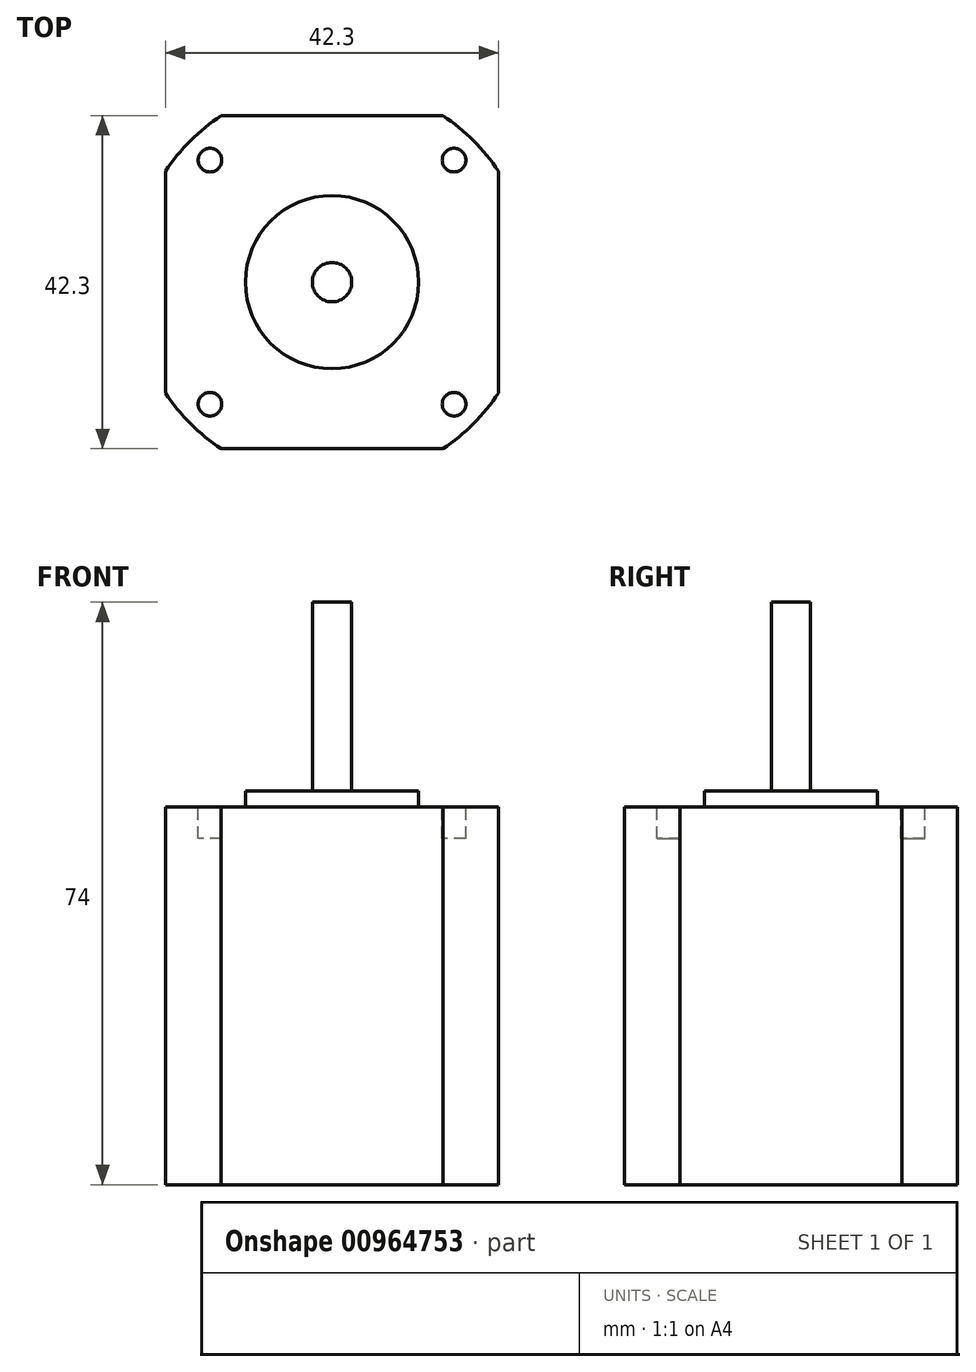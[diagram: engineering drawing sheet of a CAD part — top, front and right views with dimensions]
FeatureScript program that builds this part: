
annotation { "Feature Type Name" : "Feature", "Feature Type Description" : "" }
export const myFeature = defineFeature(function(context is Context, id is Id, definition is map)
    precondition{}
    {
        {
            var Q0;
            Q0=qCreatedBy(makeId("Top.planeOp"),FACE);
            var sketch = newSketch(context, id + "F0", { "sketchPlane" : qUnion([Q0])});
            skLineSegment(sketch, "E0.bottom", {"start": v(14.08, 21.15) * mm, "end": v(-14.08, 21.15) * mm});
            skLineSegment(sketch, "E0.top", {"start": v(14.08, -21.15) * mm, "end": v(-14.08, -21.15) * mm});
            skLineSegment(sketch, "E0.left", {"start": v(21.15, 14.08) * mm, "end": v(21.15, -14.08) * mm});
            skLineSegment(sketch, "E0.right", {"start": v(-21.15, 14.08) * mm, "end": v(-21.15, -14.08) * mm});
            skPoint(sketch, "E0.middle", {"position": v(0, 0) * mm});
            skArc(sketch, "E1", {"start": v(-14.08, 21.15) * mm, "mid": v(-17.97, 17.97) * mm, "end": v(-21.15, 14.08) * mm});
            skPoint(sketch, "E2", {"position": v(14.08, 21.15) * mm});
            skPoint(sketch, "E3", {"position": v(21.15, 14.08) * mm});
            skArc(sketch, "E4.trimOffspring", {"start": v(-21.15, -14.08) * mm, "mid": v(-17.97, -17.97) * mm, "end": v(-14.08, -21.15) * mm});
            skArc(sketch, "E5.trimOffspring", {"start": v(14.08, -21.15) * mm, "mid": v(17.97, -17.97) * mm, "end": v(21.15, -14.08) * mm});
            skArc(sketch, "E6.trimOffspring", {"start": v(21.15, 14.08) * mm, "mid": v(17.97, 17.97) * mm, "end": v(14.08, 21.15) * mm});
            skSolve(sketch);
        }
        {
            var Q0;
            Q0 = qSketchRegion(id + "F0", true);
            extrude(context, id + "F1", {"entities" : qUnion([Q0]), "depth" : 48 * mm, "offsetDistance" : 25.4 * mm});
        }
        {
            var Q0;
            Q0=makeQuery(id+"F1.opExtrude","CAP_FACE",FACE,{"disambiguationData":[OSD([sQuery(id+"F0.wireOp",EDGE,"E0.bottom"),sQuery(id+"F0.wireOp",EDGE,"E0.top"),sQuery(id+"F0.wireOp",EDGE,"E0.left"),sQuery(id+"F0.wireOp",EDGE,"E0.right"),sQuery(id+"F0.wireOp",EDGE,"E1"),sQuery(id+"F0.wireOp",EDGE,"E4.trimOffspring"),sQuery(id+"F0.wireOp",EDGE,"E5.trimOffspring"),sQuery(id+"F0.wireOp",EDGE,"E6.trimOffspring")])],"isStart":false});
            var sketch = newSketch(context, id + "F2", { "sketchPlane" : qUnion([Q0])});
            skCircle(sketch, "E7", {"center": v(0, 0) * mm, "radius": 11 * mm});
            skSolve(sketch);
        }
        {
            var Q0;
            Q0 = qSketchRegion(id + "F2", true);
            extrude(context, id + "F3", {"entities" : qUnion([Q0]), "operationType" : NewBodyOperationType.ADD, "depth" : 2 * mm, "offsetDistance" : 25.4 * mm});
        }
        {
            var Q0;
            Q0=makeQuery(id+"F3.opExtrude","CAP_FACE",FACE,{"disambiguationData":[OSD([sQuery(id+"F2.wireOp",EDGE,"E7")])],"isStart":false});
            var sketch = newSketch(context, id + "F4", { "sketchPlane" : qUnion([Q0])});
            skCircle(sketch, "E8", {"center": v(0, 0) * mm, "radius": 2.5 * mm});
            skSolve(sketch);
        }
        {
            var Q0;
            Q0 = qSketchRegion(id + "F4", true);
            extrude(context, id + "F5", {"entities" : qUnion([Q0]), "operationType" : NewBodyOperationType.ADD, "depth" : 24 * mm, "offsetDistance" : 25.4 * mm});
        }
        {
            var Q0;
            Q0=makeQuery(id+"F1.opExtrude","CAP_FACE",FACE,{"disambiguationData":[OSD([sQuery(id+"F0.wireOp",EDGE,"E0.bottom"),sQuery(id+"F0.wireOp",EDGE,"E0.top"),sQuery(id+"F0.wireOp",EDGE,"E0.left"),sQuery(id+"F0.wireOp",EDGE,"E0.right"),sQuery(id+"F0.wireOp",EDGE,"E1"),sQuery(id+"F0.wireOp",EDGE,"E4.trimOffspring"),sQuery(id+"F0.wireOp",EDGE,"E5.trimOffspring"),sQuery(id+"F0.wireOp",EDGE,"E6.trimOffspring")])],"isStart":false});
            var sketch = newSketch(context, id + "F6", { "sketchPlane" : qUnion([Q0])});
            skLineSegment(sketch, "E9.bottom", {"start": v(-15.5, 15.5) * mm, "end": v(15.5, 15.5) * mm, "construction": true});
            skLineSegment(sketch, "E9.top", {"start": v(-15.5, -15.5) * mm, "end": v(15.5, -15.5) * mm, "construction": true});
            skLineSegment(sketch, "E9.left", {"start": v(-15.5, 15.5) * mm, "end": v(-15.5, -15.5) * mm, "construction": true});
            skLineSegment(sketch, "E9.right", {"start": v(15.5, 15.5) * mm, "end": v(15.5, -15.5) * mm, "construction": true});
            skPoint(sketch, "E9.middle", {"position": v(0, 0) * mm});
            skCircle(sketch, "E10", {"center": v(-15.5, -15.5) * mm, "radius": 1.5 * mm});
            skCircle(sketch, "E11", {"center": v(15.5, -15.5) * mm, "radius": 1.5 * mm});
            skCircle(sketch, "E12", {"center": v(15.5, 15.5) * mm, "radius": 1.5 * mm});
            skCircle(sketch, "E13", {"center": v(-15.5, 15.5) * mm, "radius": 1.5 * mm});
            skSolve(sketch);
        }
        {
            var Q0;
            Q0 = qSketchRegion(id + "F6", true);
            extrude(context, id + "F7", {"entities" : qUnion([Q0]), "operationType" : NewBodyOperationType.REMOVE, "oppositeDirection" : true, "depth" : 4 * mm, "offsetDistance" : 25.4 * mm});
        }
    });
